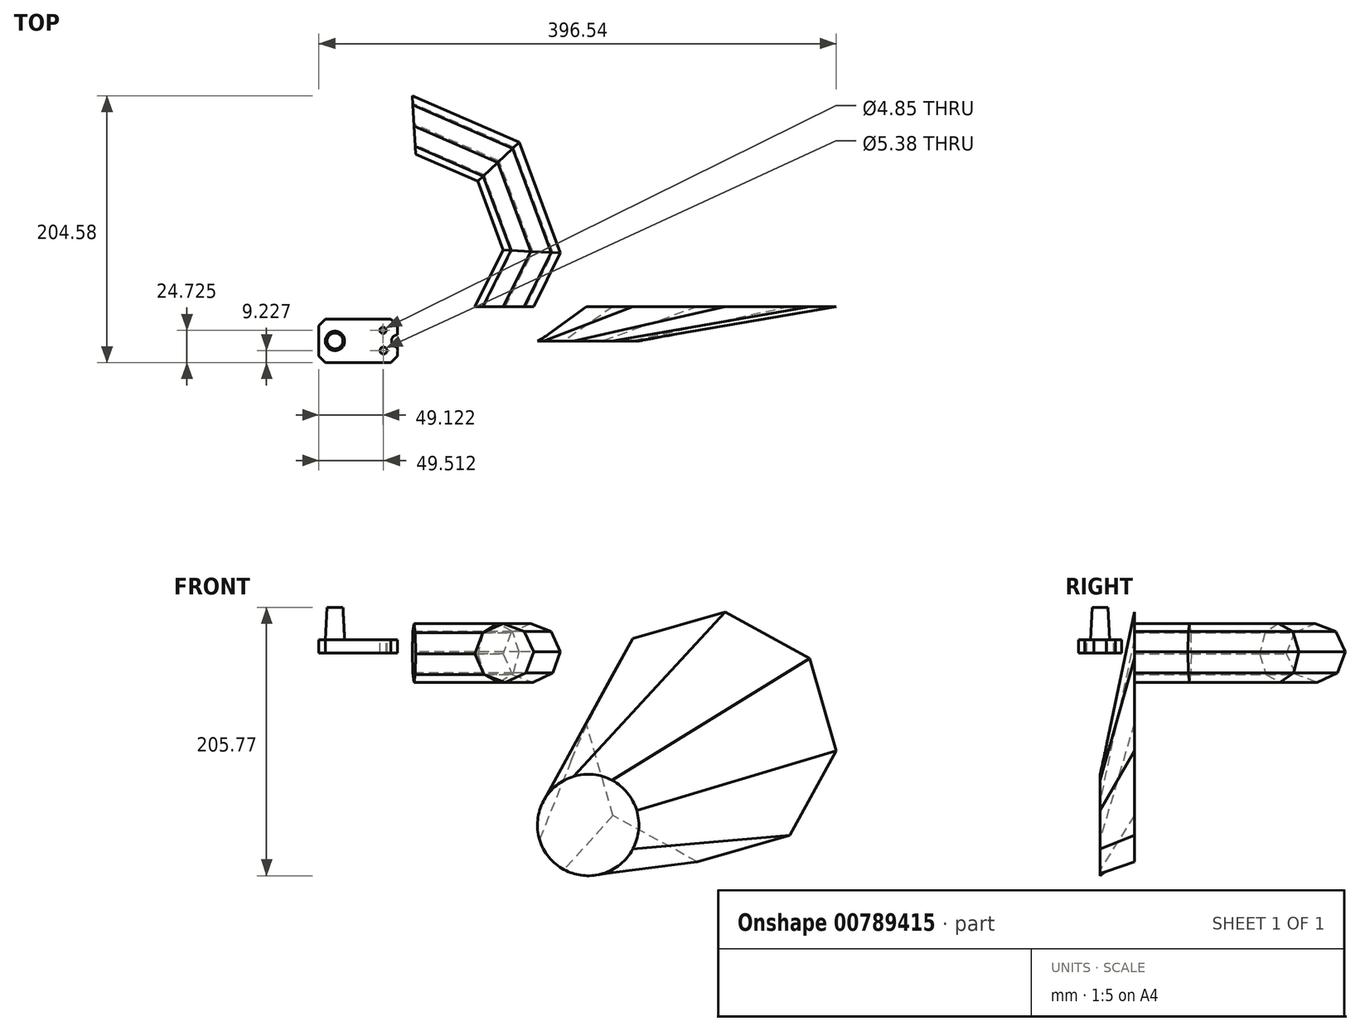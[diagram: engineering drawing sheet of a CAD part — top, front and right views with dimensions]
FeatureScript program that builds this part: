
annotation { "Feature Type Name" : "Feature", "Feature Type Description" : "" }
export const myFeature = defineFeature(function(context is Context, id is Id, definition is map)
    precondition{}
    {
        {
            var Q0;
            Q0=qCreatedBy(makeId("Top.planeOp"),FACE);
            var sketch = newSketch(context, id + "F0", { "sketchPlane" : qUnion([Q0])});
            skLineSegment(sketch, "E0.bottom", {"start": v(-30.1, 16.6) * mm, "end": v(30.1, 16.6) * mm});
            skLineSegment(sketch, "E0.top", {"start": v(-30.1, -16.6) * mm, "end": v(30.1, -16.6) * mm});
            skLineSegment(sketch, "E0.left", {"start": v(-30.1, 16.6) * mm, "end": v(-30.1, -16.6) * mm});
            skLineSegment(sketch, "E0.right", {"start": v(30.1, 16.6) * mm, "end": v(30.1, -16.6) * mm});
            skPoint(sketch, "E0.middle", {"position": v(0, 0) * mm});
            skSolve(sketch);
        }
        {
            var Q0;
            Q0=makeQuery(id+"F0.imprint","IMPRINT",FACE,{"disambiguationData":[TD([[makeQuery(id+"F0.imprint","IMPRINT",EDGE,{"derivedFrom":sQuery(id+"F0.wireOp",EDGE,"E0.bottom")}),-1.0]])]});
            extrude(context, id + "F1", {"entities" : qUnion([Q0]), "depth" : 10 * mm, "offsetDistance" : 25 * mm});
        }
        {
            var Q0;
            Q0=makeQuery(id+"F1.opExtrude","CAP_FACE",FACE,{"disambiguationData":[OSD([sQuery(id+"F0.wireOp",EDGE,"E0.bottom"),sQuery(id+"F0.wireOp",EDGE,"E0.top"),sQuery(id+"F0.wireOp",EDGE,"E0.left"),sQuery(id+"F0.wireOp",EDGE,"E0.right")])],"isStart":false});
            var sketch = newSketch(context, id + "F2", { "sketchPlane" : qUnion([Q0])});
            skCircle(sketch, "E1", {"center": v(19.03, 8.12) * mm, "radius": 2.43 * mm});
            skCircle(sketch, "E2", {"center": v(19.42, -7.38) * mm, "radius": 2.7 * mm});
            skCircle(sketch, "E3", {"center": v(30.1, 0) * mm, "radius": 2.83 * mm});
            skSolve(sketch);
        }
        {
            var Q0;
            Q0=makeQuery(id+"F2.imprint","IMPRINT",FACE,{"disambiguationData":[TD([[makeQuery(id+"F2.imprint","IMPRINT",EDGE,{"derivedFrom":sQuery(id+"F2.wireOp",EDGE,"E2")}),1.0]])]});
            var Q1;
            Q1=makeQuery(id+"F2.imprint","IMPRINT",FACE,{"disambiguationData":[TD([[makeQuery(id+"F2.imprint","IMPRINT",EDGE,{"derivedFrom":sQuery(id+"F2.wireOp",EDGE,"E1")}),1.0]])]});
            extrude(context, id + "F3", {"entities" : qUnion([Q0, Q1]), "operationType" : NewBodyOperationType.REMOVE, "oppositeDirection" : true, "depth" : 10 * mm, "offsetDistance" : 25 * mm});
        }
        {
            var Q0;
            Q0=makeQuery(id+"F1.opExtrude","CAP_FACE",FACE,{"disambiguationData":[OSD([sQuery(id+"F0.wireOp",EDGE,"E0.bottom"),sQuery(id+"F0.wireOp",EDGE,"E0.top"),sQuery(id+"F0.wireOp",EDGE,"E0.left"),sQuery(id+"F0.wireOp",EDGE,"E0.right")])],"isStart":false});
            var sketch = newSketch(context, id + "F4", { "sketchPlane" : qUnion([Q0])});
            skCircle(sketch, "E4", {"center": v(-17.78, 0) * mm, "radius": 7.4 * mm});
            skSolve(sketch);
        }
        {
            var Q0;
            Q0=makeQuery(id+"F4.imprint","IMPRINT",FACE,{"disambiguationData":[TD([[makeQuery(id+"F4.imprint","IMPRINT",EDGE,{"derivedFrom":sQuery(id+"F4.wireOp",EDGE,"E4")}),1.0]])]});
            var Q1;
            Q1=sQuery(id+"F4.wireOp",EDGE,"E4");
            extrude(context, id + "F5", {"entities" : qUnion([Q0]), "operationType" : NewBodyOperationType.ADD, "surfaceEntities" : qUnion([Q1]), "depth" : 25 * mm, "offsetDistance" : 25 * mm, "hasDraft" : true, "draftAngle" : 3 * degree, "draftPullDirection" : true});
        }
        {
            var Q0;
            Q0=makeQuery(id+"F1.opExtrude","SWEPT_EDGE",EDGE,{"disambiguationData":[OSD([sQuery(id+"F0.wireOp",EDGE,"E0.top"),sQuery(id+"F0.wireOp",EDGE,"E0.left")])]});
            var Q1;
            Q1=makeQuery(id+"F1.opExtrude","SWEPT_EDGE",EDGE,{"disambiguationData":[OSD([sQuery(id+"F0.wireOp",EDGE,"E0.bottom"),sQuery(id+"F0.wireOp",EDGE,"E0.right")])]});
            var Q2;
            Q2=makeQuery(id+"F1.opExtrude","SWEPT_EDGE",EDGE,{"disambiguationData":[OSD([sQuery(id+"F0.wireOp",EDGE,"E0.top"),sQuery(id+"F0.wireOp",EDGE,"E0.right")])]});
            var Q3;
            Q3=makeQuery(id+"F1.opExtrude","SWEPT_EDGE",EDGE,{"disambiguationData":[OSD([sQuery(id+"F0.wireOp",EDGE,"E0.bottom"),sQuery(id+"F0.wireOp",EDGE,"E0.left")])]});
            chamfer(context, id + "F6", {"entities" : qUnion([Q0, Q1, Q2, Q3]), "width" : 5 * mm, "tangentPropagation" : true});
        }
        {
            var Q0;
            Q0=makeQuery(id+"F1.opExtrude","CAP_FACE",FACE,{"disambiguationData":[OSD([sQuery(id+"F0.wireOp",EDGE,"E0.bottom"),sQuery(id+"F0.wireOp",EDGE,"E0.top"),sQuery(id+"F0.wireOp",EDGE,"E0.left"),sQuery(id+"F0.wireOp",EDGE,"E0.right")])],"isStart":false});
            var sketch = newSketch(context, id + "F7", { "sketchPlane" : qUnion([Q0])});
            skCircle(sketch, "E5", {"center": v(30.1, 0) * mm, "radius": 4.61 * mm});
            skSolve(sketch);
        }
        {
            var Q0;
            {var subQ0=sQuery(id+"F7.wireOp",EDGE,"E5");var subQ1=makeQuery(id+"F1.opExtrude","CAP_EDGE",EDGE,{"disambiguationData":[OSD([sQuery(id+"F0.wireOp",EDGE,"E0.right")])],"isStart":false});var subQ2=makeQuery(id+"F7.imprint","INTERSECT",VERTEX,{"disambiguationData":[OD(0.0)],"derivedFrom":[subQ1,subQ0]});Q0=makeQuery(id+"F7.imprint","IMPRINT",FACE,{"disambiguationData":[TD([[makeQuery(id+"F7.imprint","IMPRINT",EDGE,{"disambiguationData":[TD([[subQ2,-1.0]])],"derivedFrom":subQ0}),1.0]])]});}
            var Q1;
            Q1=sQuery(id+"F7.wireOp",EDGE,"E5");
            extrude(context, id + "F8", {"entities" : qUnion([Q0]), "operationType" : NewBodyOperationType.REMOVE, "surfaceEntities" : qUnion([Q1]), "oppositeDirection" : true, "depth" : 10 * mm, "offsetDistance" : 25 * mm});
        }
        {
            var Q0;
            Q0=qCreatedBy(makeId("Top.planeOp"),FACE);
            var sketch = newSketch(context, id + "F9", { "sketchPlane" : qUnion([Q0])});
            skLineSegment(sketch, "E6", {"start": v(110.84, 26.26) * mm, "end": v(132.06, 68.62) * mm});
            skLineSegment(sketch, "E7", {"start": v(132.06, 68.62) * mm, "end": v(106.73, 136.69) * mm});
            skLineSegment(sketch, "E8", {"start": v(106.73, 136.69) * mm, "end": v(42.85, 164.45) * mm});
            skSolve(sketch);
        }
        {
            var Q0;
            Q0=sQuery(id+"F9.wireOp",VERTEX,"E6.start");
            var Q1;
            Q1=qCreatedBy(makeId("Front.planeOp"),FACE);
            cPlane(context, id + "F10", {"entities" : qUnion([Q0, Q1]), "cplaneType" : CPlaneType.PLANE_POINT, "offset" : 25 * mm, "width" : 150 * mm, "height" : 150 * mm});
        }
        {
            var Q0;
            Q0=qCreatedBy(id+"F10.planeOp",FACE);
            var sketch = newSketch(context, id + "F11", { "sketchPlane" : qUnion([Q0])});
            skCircle(sketch, "E9.cCircle", {"center": v(111.86, 0) * mm, "radius": 20.84 * mm, "construction": true});
            skLineSegment(sketch, "E9.0", {"start": v(128.36, -15.38) * mm, "end": v(112.66, -22.54) * mm});
            skLineSegment(sketch, "E9.1", {"start": v(112.66, -22.54) * mm, "end": v(96.49, -16.5) * mm});
            skLineSegment(sketch, "E9.2", {"start": v(96.49, -16.5) * mm, "end": v(89.32, -0.8) * mm});
            skLineSegment(sketch, "E9.3", {"start": v(89.32, -0.8) * mm, "end": v(95.36, 15.38) * mm});
            skLineSegment(sketch, "E9.4", {"start": v(95.36, 15.38) * mm, "end": v(111.06, 22.54) * mm});
            skLineSegment(sketch, "E9.5", {"start": v(111.06, 22.54) * mm, "end": v(127.24, 16.5) * mm});
            skLineSegment(sketch, "E9.6", {"start": v(127.24, 16.5) * mm, "end": v(134.4, 0.8) * mm});
            skLineSegment(sketch, "E9.7", {"start": v(134.4, 0.8) * mm, "end": v(128.36, -15.38) * mm});
            skPoint(sketch, "E9.0.midPoint", {"position": v(120.5, -18.96) * mm});
            skSolve(sketch);
        }
        {
            var Q0;
            Q0=makeQuery(id+"F11.imprint","IMPRINT",FACE,{"disambiguationData":[TD([[makeQuery(id+"F11.imprint","IMPRINT",EDGE,{"derivedFrom":sQuery(id+"F11.wireOp",EDGE,"E9.0")}),-1.0]])]});
            var Q1;
            Q1=sQuery(id+"F9.wireOp",EDGE,"E6");
            var Q2;
            Q2=sQuery(id+"F9.wireOp",EDGE,"E7");
            var Q3;
            Q3=sQuery(id+"F9.wireOp",EDGE,"E8");
            sweep(context, id + "F12", {"profiles" : qUnion([Q0]), "path" : qUnion([Q1, Q2, Q3])});
        }
        {
            var Q0;
            Q0=qCreatedBy(makeId("Front.planeOp"),FACE);
            var sketch = newSketch(context, id + "F13", { "sketchPlane" : qUnion([Q0])});
            skCircle(sketch, "E10", {"center": v(176.24, -131.9) * mm, "radius": 38.87 * mm});
            skSolve(sketch);
        }
        {
            var Q0;
            Q0=qCreatedBy(id+"F10.planeOp",FACE);
            var sketch = newSketch(context, id + "F14", { "sketchPlane" : qUnion([Q0])});
            skCircle(sketch, "E11.cCircle", {"center": v(270.59, -64.35) * mm, "radius": 89.1 * mm, "construction": true});
            skLineSegment(sketch, "E11.0", {"start": v(366.45, -74.97) * mm, "end": v(330.86, -139.65) * mm});
            skLineSegment(sketch, "E11.1", {"start": v(330.86, -139.65) * mm, "end": v(259.97, -160.21) * mm});
            skLineSegment(sketch, "E11.2", {"start": v(259.97, -160.21) * mm, "end": v(195.3, -124.63) * mm});
            skLineSegment(sketch, "E11.3", {"start": v(195.3, -124.63) * mm, "end": v(174.73, -53.73) * mm});
            skLineSegment(sketch, "E11.4", {"start": v(174.73, -53.73) * mm, "end": v(210.31, 10.94) * mm});
            skLineSegment(sketch, "E11.5", {"start": v(210.31, 10.94) * mm, "end": v(281.2, 31.5) * mm});
            skLineSegment(sketch, "E11.6", {"start": v(281.2, 31.5) * mm, "end": v(345.88, -4.08) * mm});
            skLineSegment(sketch, "E11.7", {"start": v(345.88, -4.08) * mm, "end": v(366.45, -74.97) * mm});
            skPoint(sketch, "E11.0.midPoint", {"position": v(348.66, -107.3) * mm});
            skSolve(sketch);
        }
        {
            var Q0;
            Q0=makeQuery(id+"F14.imprint","IMPRINT",FACE,{"disambiguationData":[TD([[makeQuery(id+"F14.imprint","IMPRINT",EDGE,{"derivedFrom":sQuery(id+"F14.wireOp",EDGE,"E11.0")}),-1.0]])]});
            var Q1;
            Q1=makeQuery(id+"F13.imprint","IMPRINT",FACE,{"disambiguationData":[TD([[makeQuery(id+"F13.imprint","IMPRINT",EDGE,{"derivedFrom":sQuery(id+"F13.wireOp",EDGE,"E10")}),1.0]])]});
            loft(context, id + "F15", {"sheetProfilesArray" : [{ "sheetProfileEntities" : qUnion([Q0]) }, { "sheetProfileEntities" : qUnion([Q1]) }]});
        }
    });
